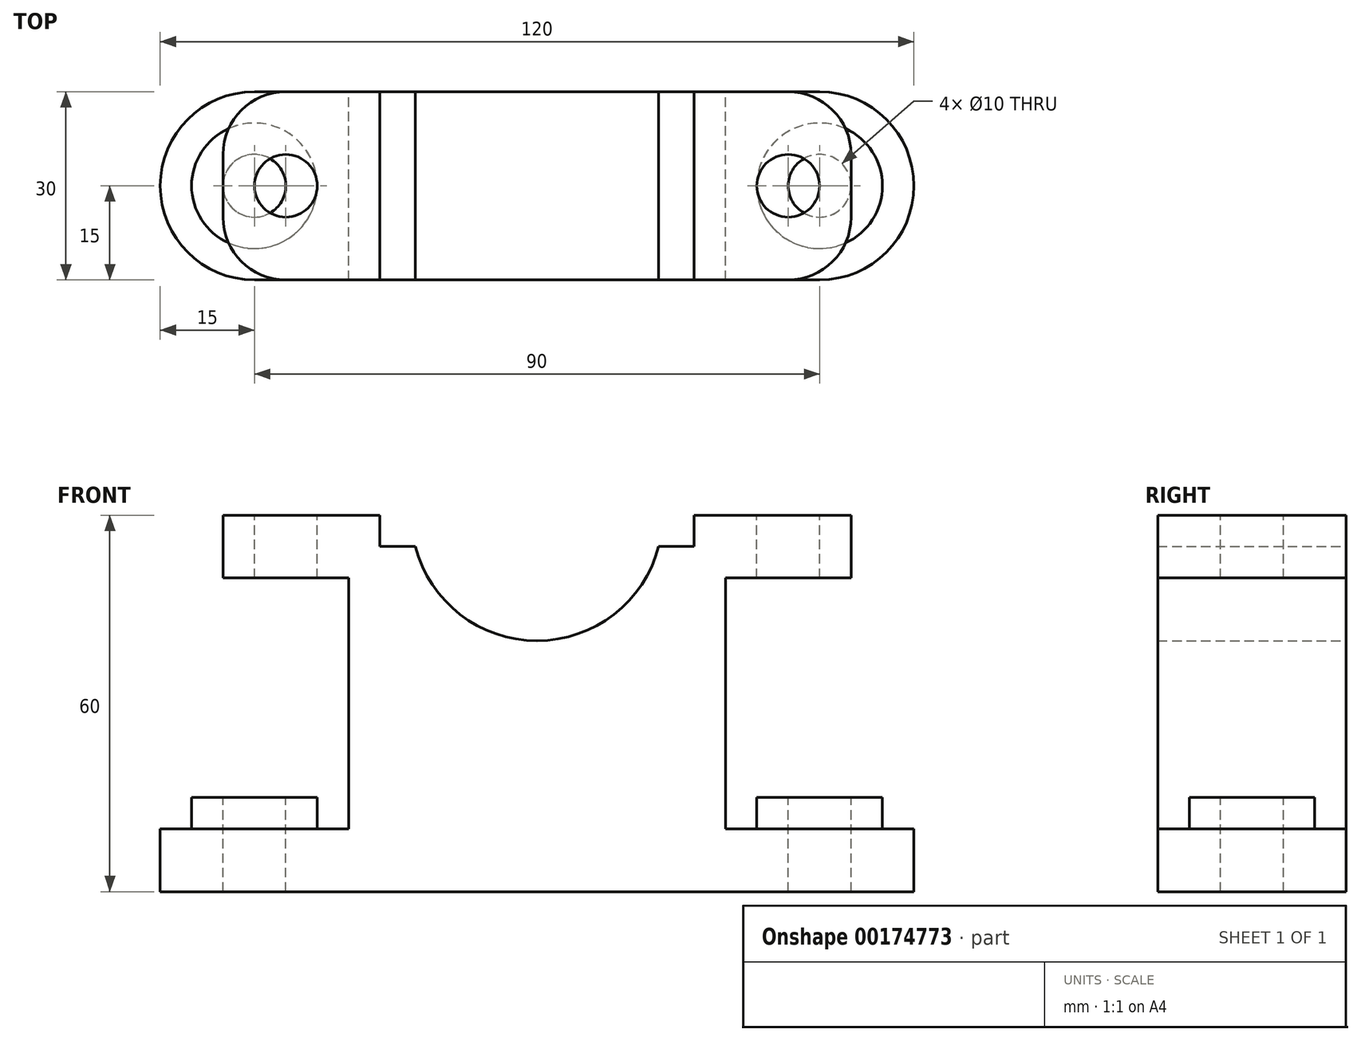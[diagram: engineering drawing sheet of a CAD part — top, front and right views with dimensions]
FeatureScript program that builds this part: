
annotation { "Feature Type Name" : "Feature", "Feature Type Description" : "" }
export const myFeature = defineFeature(function(context is Context, id is Id, definition is map)
    precondition{}
    {
        {
            var Q0;
            Q0=qCreatedBy(makeId("Front.planeOp"),FACE);
            var sketch = newSketch(context, id + "F0", { "sketchPlane" : qUnion([Q0])});
            skLineSegment(sketch, "E0", {"start": v(-60, 0) * mm, "end": v(60, 0) * mm});
            skLineSegment(sketch, "E1", {"start": v(60, 0) * mm, "end": v(60, 10) * mm});
            skLineSegment(sketch, "E2", {"start": v(60, 10) * mm, "end": v(30, 10) * mm});
            skLineSegment(sketch, "E3", {"start": v(30, 10) * mm, "end": v(30, 50) * mm});
            skLineSegment(sketch, "E4", {"start": v(30, 50) * mm, "end": v(50, 50) * mm});
            skLineSegment(sketch, "E5", {"start": v(50, 50) * mm, "end": v(50, 60) * mm});
            skLineSegment(sketch, "E6", {"start": v(50, 60) * mm, "end": v(25, 60) * mm});
            skLineSegment(sketch, "E7", {"start": v(-50, 60) * mm, "end": v(-50, 50) * mm});
            skLineSegment(sketch, "E8", {"start": v(-50, 50) * mm, "end": v(-30, 50) * mm});
            skLineSegment(sketch, "E9", {"start": v(-30, 50) * mm, "end": v(-30, 10) * mm});
            skLineSegment(sketch, "E10", {"start": v(-30, 10) * mm, "end": v(-60, 10) * mm});
            skLineSegment(sketch, "E11", {"start": v(-60, 10) * mm, "end": v(-60, 0) * mm});
            skArc(sketch, "E12", {"start": v(-19.36, 55) * mm, "mid": v(0, 40) * mm, "end": v(19.36, 55) * mm});
            skLineSegment(sketch, "E13.trimOffspring", {"start": v(-25, 60) * mm, "end": v(-50, 60) * mm});
            skLineSegment(sketch, "E14.top", {"start": v(-25, 55) * mm, "end": v(-19.36, 55) * mm});
            skLineSegment(sketch, "E14.left", {"start": v(-25, 60) * mm, "end": v(-25, 55) * mm});
            skLineSegment(sketch, "E14.right", {"start": v(25, 60) * mm, "end": v(25, 55) * mm});
            skLineSegment(sketch, "E15.trimOffspring", {"start": v(19.36, 55) * mm, "end": v(25, 55) * mm});
            skSolve(sketch);
        }
        {
            var Q0;
            Q0=makeQuery(id+"F0.imprint","IMPRINT",FACE,{"disambiguationData":[TD([[makeQuery(id+"F0.imprint","IMPRINT",EDGE,{"derivedFrom":sQuery(id+"F0.wireOp",EDGE,"E0")}),1.0]])]});
            extrude(context, id + "F1", {"entities" : qUnion([Q0]), "endBound" : BoundingType.SYMMETRIC, "depth" : 30 * mm});
        }
        {
            var Q0;
            Q0=makeQuery(id+"F1.opExtrude","CAP_EDGE",EDGE,{"disambiguationData":[OSD([sQuery(id+"F0.wireOp",EDGE,"E7")])],"isStart":false});
            var Q1;
            Q1=makeQuery(id+"F1.opExtrude","CAP_EDGE",EDGE,{"disambiguationData":[OSD([sQuery(id+"F0.wireOp",EDGE,"E5")])],"isStart":false});
            var Q2;
            Q2=makeQuery(id+"F1.opExtrude","CAP_EDGE",EDGE,{"disambiguationData":[OSD([sQuery(id+"F0.wireOp",EDGE,"E5")])],"isStart":true});
            var Q3;
            Q3=makeQuery(id+"F1.opExtrude","CAP_EDGE",EDGE,{"disambiguationData":[OSD([sQuery(id+"F0.wireOp",EDGE,"E7")])],"isStart":true});
            fillet(context, id + "F2", {"entities" : qUnion([Q0, Q1, Q2, Q3]), "radius" : 10 * mm, "tangentPropagation" : true, "allowEdgeOverflow" : false});
        }
        {
            var Q0;
            Q0=makeQuery(id+"F1.opExtrude","CAP_EDGE",EDGE,{"disambiguationData":[OSD([sQuery(id+"F0.wireOp",EDGE,"E1")])],"isStart":true});
            var Q1;
            Q1=makeQuery(id+"F1.opExtrude","CAP_EDGE",EDGE,{"disambiguationData":[OSD([sQuery(id+"F0.wireOp",EDGE,"E11")])],"isStart":true});
            var Q2;
            Q2=makeQuery(id+"F1.opExtrude","CAP_EDGE",EDGE,{"disambiguationData":[OSD([sQuery(id+"F0.wireOp",EDGE,"E11")])],"isStart":false});
            var Q3;
            Q3=makeQuery(id+"F1.opExtrude","CAP_EDGE",EDGE,{"disambiguationData":[OSD([sQuery(id+"F0.wireOp",EDGE,"E1")])],"isStart":false});
            fillet(context, id + "F3", {"entities" : qUnion([Q0, Q1, Q2, Q3]), "radius" : 15 * mm, "tangentPropagation" : true, "allowEdgeOverflow" : false});
        }
        {
            var Q0;
            Q0=makeQuery(id+"F1.opExtrude","SWEPT_FACE",FACE,{"disambiguationData":[OSD([sQuery(id+"F0.wireOp",EDGE,"E13.trimOffspring")])]});
            var sketch = newSketch(context, id + "F4", { "sketchPlane" : qUnion([Q0])});
            skCircle(sketch, "E16", {"center": v(-40, 0) * mm, "radius": 5 * mm});
            skCircle(sketch, "E17", {"center": v(40, 0) * mm, "radius": 5 * mm});
            skSolve(sketch);
        }
        {
            var Q0;
            Q0=makeQuery(id+"F4.imprint","IMPRINT",FACE,{"disambiguationData":[TD([[makeQuery(id+"F4.imprint","IMPRINT",EDGE,{"derivedFrom":sQuery(id+"F4.wireOp",EDGE,"E17")}),1.0]])]});
            var Q1;
            Q1=makeQuery(id+"F4.imprint","IMPRINT",FACE,{"disambiguationData":[TD([[makeQuery(id+"F4.imprint","IMPRINT",EDGE,{"derivedFrom":sQuery(id+"F4.wireOp",EDGE,"E16")}),1.0]])]});
            extrude(context, id + "F5", {"entities" : qUnion([Q0, Q1]), "operationType" : NewBodyOperationType.REMOVE, "endBound" : BoundingType.UP_TO_NEXT, "oppositeDirection" : true, "depth" : 25 * mm});
        }
        {
            var Q0;
            Q0=makeQuery(id+"F1.opExtrude","SWEPT_FACE",FACE,{"disambiguationData":[OSD([sQuery(id+"F0.wireOp",EDGE,"E2")])]});
            var sketch = newSketch(context, id + "F6", { "sketchPlane" : qUnion([Q0])});
            skCircle(sketch, "E18", {"center": v(45, 0) * mm, "radius": 10 * mm});
            skSolve(sketch);
        }
        {
            var Q0;
            Q0=makeQuery(id+"F6.imprint","IMPRINT",FACE,{"disambiguationData":[TD([[makeQuery(id+"F6.imprint","IMPRINT",EDGE,{"derivedFrom":sQuery(id+"F6.wireOp",EDGE,"E18")}),1.0]])]});
            extrude(context, id + "F7", {"entities" : qUnion([Q0]), "operationType" : NewBodyOperationType.ADD, "depth" : 5 * mm});
        }
        {
            var Q0;
            Q0=makeQuery(id+"F1.opExtrude","SWEPT_FACE",FACE,{"disambiguationData":[OSD([sQuery(id+"F0.wireOp",EDGE,"E10")])]});
            var sketch = newSketch(context, id + "F8", { "sketchPlane" : qUnion([Q0])});
            skCircle(sketch, "E19", {"center": v(-45, 0) * mm, "radius": 10 * mm});
            skSolve(sketch);
        }
        {
            var Q0;
            Q0=makeQuery(id+"F8.imprint","IMPRINT",FACE,{"disambiguationData":[TD([[makeQuery(id+"F8.imprint","IMPRINT",EDGE,{"derivedFrom":sQuery(id+"F8.wireOp",EDGE,"E19")}),1.0]])]});
            extrude(context, id + "F9", {"entities" : qUnion([Q0]), "operationType" : NewBodyOperationType.ADD, "depth" : 5 * mm});
        }
        {
            var Q0;
            Q0=makeQuery(id+"F9.opExtrude","CAP_FACE",FACE,{"disambiguationData":[OSD([sQuery(id+"F8.wireOp",EDGE,"E19")])],"isStart":false});
            var sketch = newSketch(context, id + "F10", { "sketchPlane" : qUnion([Q0])});
            skPoint(sketch, "E20", {"position": v(-45, 0) * mm});
            skSolve(sketch);
        }
        {
            var Q0;
            Q0=makeQuery(id+"F7.opExtrude","CAP_FACE",FACE,{"disambiguationData":[OSD([sQuery(id+"F6.wireOp",EDGE,"E18")])],"isStart":false});
            var sketch = newSketch(context, id + "F11", { "sketchPlane" : qUnion([Q0])});
            skPoint(sketch, "E21", {"position": v(45, 0) * mm});
            skSolve(sketch);
        }
        {
            var Q0;
            Q0=sQuery(id+"F10.wireOp",VERTEX,"E20");
            var Q1;
            Q1=sQuery(id+"F11.wireOp",VERTEX,"E21");
            var Q2;
            Q2=makeQuery(id+"F1.opExtrude","SWEPT_BODY",BODY,{"disambiguationData":[OSD([sQuery(id+"F0.wireOp",EDGE,"E0"),sQuery(id+"F0.wireOp",EDGE,"E1"),sQuery(id+"F0.wireOp",EDGE,"E2"),sQuery(id+"F0.wireOp",EDGE,"E3"),sQuery(id+"F0.wireOp",EDGE,"E4"),sQuery(id+"F0.wireOp",EDGE,"E5"),sQuery(id+"F0.wireOp",EDGE,"E6"),sQuery(id+"F0.wireOp",EDGE,"E7"),sQuery(id+"F0.wireOp",EDGE,"E8"),sQuery(id+"F0.wireOp",EDGE,"E9"),sQuery(id+"F0.wireOp",EDGE,"E10"),sQuery(id+"F0.wireOp",EDGE,"E11"),sQuery(id+"F0.wireOp",EDGE,"E12"),sQuery(id+"F0.wireOp",EDGE,"E13.trimOffspring"),sQuery(id+"F0.wireOp",EDGE,"E14.top"),sQuery(id+"F0.wireOp",EDGE,"E14.left"),sQuery(id+"F0.wireOp",EDGE,"E14.right"),sQuery(id+"F0.wireOp",EDGE,"E15.trimOffspring")])]});
            hole(context, id + "F12", {"style" : HoleStyle.SIMPLE, "endStyle" : HoleEndStyle.THROUGH, "holeDiameter" : 10 * mm, "locations" : qUnion([Q0, Q1]), "scope" : qUnion([Q2]), "isTappedThrough" : true});
        }
    });
